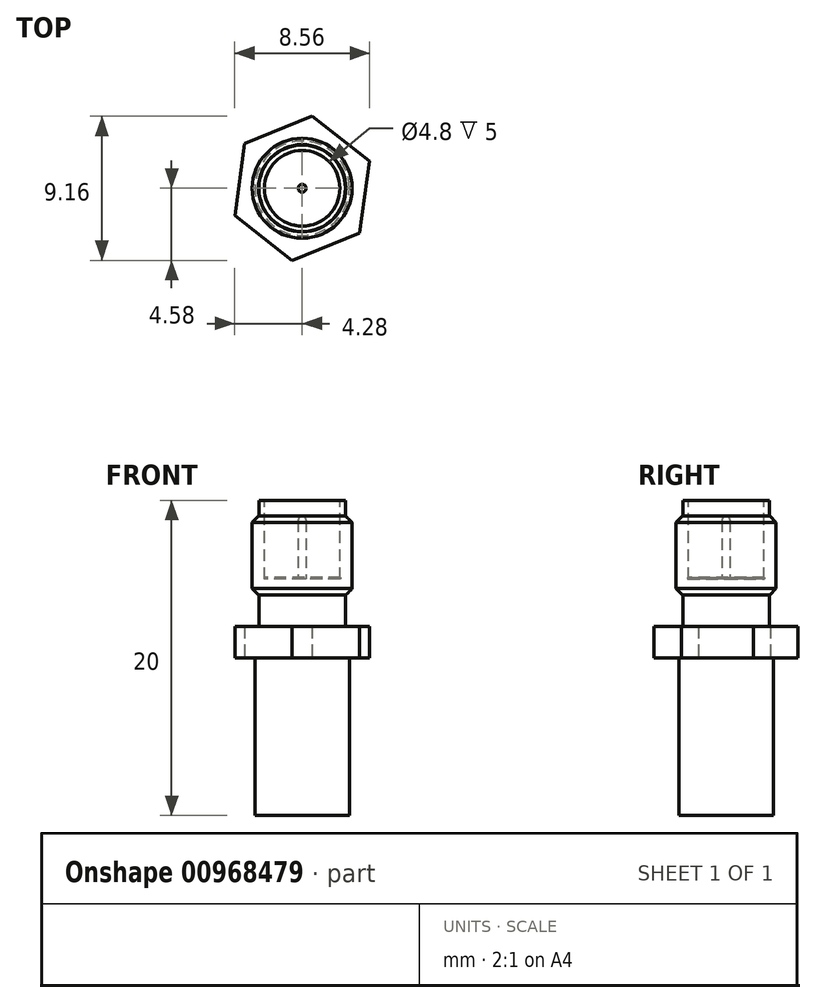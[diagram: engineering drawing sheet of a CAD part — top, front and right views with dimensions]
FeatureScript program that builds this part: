
annotation { "Feature Type Name" : "Feature", "Feature Type Description" : "" }
export const myFeature = defineFeature(function(context is Context, id is Id, definition is map)
    precondition{}
    {
        {
            var Q0;
            Q0=qCreatedBy(makeId("Top.planeOp"),FACE);
            var sketch = newSketch(context, id + "F0", { "sketchPlane" : qUnion([Q0])});
            skCircle(sketch, "E0.cCircle", {"center": v(0, 0) * mm, "radius": 4 * mm, "construction": true});
            skLineSegment(sketch, "E0.0", {"start": v(-3.65, 2.83) * mm, "end": v(0.63, 4.58) * mm});
            skLineSegment(sketch, "E0.1", {"start": v(0.63, 4.58) * mm, "end": v(4.28, 1.74) * mm});
            skLineSegment(sketch, "E0.2", {"start": v(4.28, 1.74) * mm, "end": v(3.65, -2.83) * mm});
            skLineSegment(sketch, "E0.3", {"start": v(3.65, -2.83) * mm, "end": v(-0.63, -4.58) * mm});
            skLineSegment(sketch, "E0.4", {"start": v(-0.63, -4.58) * mm, "end": v(-4.28, -1.74) * mm});
            skLineSegment(sketch, "E0.5", {"start": v(-4.28, -1.74) * mm, "end": v(-3.65, 2.83) * mm});
            skPoint(sketch, "E0.0.midPoint", {"position": v(-1.5, 3.7) * mm});
            skSolve(sketch);
        }
        {
            var Q0;
            Q0 = qSketchRegion(id + "F0", true);
            extrude(context, id + "F1", {"entities" : qUnion([Q0]), "depth" : 2 * mm, "offsetDistance" : 25 * mm});
        }
        {
            var Q0;
            Q0=makeQuery(id+"F1.opExtrude","CAP_FACE",FACE,{"disambiguationData":[OSD([sQuery(id+"F0.wireOp",EDGE,"E0.0"),sQuery(id+"F0.wireOp",EDGE,"E0.1"),sQuery(id+"F0.wireOp",EDGE,"E0.2"),sQuery(id+"F0.wireOp",EDGE,"E0.3"),sQuery(id+"F0.wireOp",EDGE,"E0.4"),sQuery(id+"F0.wireOp",EDGE,"E0.5")])],"isStart":false});
            var sketch = newSketch(context, id + "F2", { "sketchPlane" : qUnion([Q0])});
            skCircle(sketch, "E1", {"center": v(0, 0) * mm, "radius": 2.75 * mm});
            skSolve(sketch);
        }
        {
            var Q0;
            Q0 = qSketchRegion(id + "F2", true);
            extrude(context, id + "F3", {"entities" : qUnion([Q0]), "operationType" : NewBodyOperationType.ADD, "depth" : 2 * mm, "offsetDistance" : 25 * mm});
        }
        {
            var Q0;
            Q0=makeQuery(id+"F3.opExtrude","CAP_FACE",FACE,{"disambiguationData":[OSD([sQuery(id+"F2.wireOp",EDGE,"E1")])],"isStart":false});
            var sketch = newSketch(context, id + "F4", { "sketchPlane" : qUnion([Q0])});
            skCircle(sketch, "E2", {"center": v(0, 0) * mm, "radius": 3.17 * mm});
            skSolve(sketch);
        }
        {
            var Q0;
            Q0 = qSketchRegion(id + "F4", true);
            extrude(context, id + "F5", {"entities" : qUnion([Q0]), "operationType" : NewBodyOperationType.ADD, "depth" : 5 * mm, "offsetDistance" : 25 * mm});
        }
        {
            var Q0;
            Q0=makeQuery(id+"F5.opExtrude","CAP_FACE",FACE,{"disambiguationData":[OSD([sQuery(id+"F4.wireOp",EDGE,"E2")])],"isStart":false});
            var sketch = newSketch(context, id + "F6", { "sketchPlane" : qUnion([Q0])});
            skCircle(sketch, "E3", {"center": v(0, 0) * mm, "radius": 2.75 * mm});
            skSolve(sketch);
        }
        {
            var Q0;
            Q0 = qSketchRegion(id + "F6", true);
            extrude(context, id + "F7", {"entities" : qUnion([Q0]), "operationType" : NewBodyOperationType.ADD, "depth" : 1 * mm, "offsetDistance" : 25 * mm});
        }
        {
            var Q0;
            Q0=makeQuery(id+"F5.opExtrude","CAP_EDGE",EDGE,{"disambiguationData":[OSD([sQuery(id+"F4.wireOp",EDGE,"E2")])],"isStart":false});
            chamfer(context, id + "F8", {"entities" : qUnion([Q0]), "width" : .4 * mm, "tangentPropagation" : true});
        }
        {
            var Q0;
            Q0=makeQuery(id+"F5.opExtrude","CAP_EDGE",EDGE,{"disambiguationData":[OSD([sQuery(id+"F4.wireOp",EDGE,"E2")])],"isStart":true});
            chamfer(context, id + "F9", {"entities" : qUnion([Q0]), "width" : .4 * mm, "tangentPropagation" : true});
        }
        {
            var Q0;
            Q0=makeQuery(id+"F7.opExtrude","CAP_FACE",FACE,{"disambiguationData":[OSD([sQuery(id+"F6.wireOp",EDGE,"E3")])],"isStart":false});
            var sketch = newSketch(context, id + "F10", { "sketchPlane" : qUnion([Q0])});
            skCircle(sketch, "E4", {"center": v(0, 0) * mm, "radius": 2.4 * mm});
            skSolve(sketch);
        }
        {
            var Q0;
            Q0 = qSketchRegion(id + "F10", true);
            extrude(context, id + "F11", {"entities" : qUnion([Q0]), "operationType" : NewBodyOperationType.REMOVE, "oppositeDirection" : true, "depth" : 5 * mm, "offsetDistance" : 25 * mm});
        }
        {
            var Q0;
            Q0=makeQuery(id+"F11.boolean.opBoolean","COPY",FACE,{"derivedFrom":makeQuery(id+"F11.opExtrude","CAP_FACE",FACE,{"disambiguationData":[OSD([sQuery(id+"F10.wireOp",EDGE,"E4")])],"isStart":false})});
            var sketch = newSketch(context, id + "F12", { "sketchPlane" : qUnion([Q0])});
            skCircle(sketch, "E5", {"center": v(0, 0) * mm, "radius": 0.25 * mm});
            skSolve(sketch);
        }
        {
            var Q0;
            Q0 = qSketchRegion(id + "F12", true);
            extrude(context, id + "F13", {"entities" : qUnion([Q0]), "operationType" : NewBodyOperationType.ADD, "depth" : 4 * mm, "offsetDistance" : 25 * mm});
        }
        {
            var Q0;
            Q0=makeQuery(id+"F13.opExtrude","CAP_EDGE",EDGE,{"disambiguationData":[OSD([sQuery(id+"F12.wireOp",EDGE,"E5")])],"isStart":false});
            fillet(context, id + "F14", {"entities" : qUnion([Q0]), "radius" : .25 * mm, "tangentPropagation" : true, "allowEdgeOverflow" : false});
        }
        {
            var Q0;
            Q0=makeQuery(id+"F1.opExtrude","CAP_FACE",FACE,{"disambiguationData":[OSD([sQuery(id+"F0.wireOp",EDGE,"E0.0"),sQuery(id+"F0.wireOp",EDGE,"E0.1"),sQuery(id+"F0.wireOp",EDGE,"E0.2"),sQuery(id+"F0.wireOp",EDGE,"E0.3"),sQuery(id+"F0.wireOp",EDGE,"E0.4"),sQuery(id+"F0.wireOp",EDGE,"E0.5")])],"isStart":true});
            var sketch = newSketch(context, id + "F15", { "sketchPlane" : qUnion([Q0])});
            skCircle(sketch, "E6", {"center": v(0, 0) * mm, "radius": 3 * mm});
            skSolve(sketch);
        }
        {
            var Q0;
            Q0 = qSketchRegion(id + "F15", true);
            extrude(context, id + "F16", {"entities" : qUnion([Q0]), "depth" : 10 * mm, "offsetDistance" : 25 * mm});
        }
        {
            var Q0;
            Q0=makeQuery(id+"F11.boolean.opBoolean","COPY",FACE,{"derivedFrom":makeQuery(id+"F11.opExtrude","CAP_FACE",FACE,{"disambiguationData":[OSD([sQuery(id+"F10.wireOp",EDGE,"E4")])],"isStart":false})});
            var sketch = newSketch(context, id + "F17", { "sketchPlane" : qUnion([Q0])});
            skCircle(sketch, "E7", {"center": v(0, 0) * mm, "radius": 2.44 * mm});
            skSolve(sketch);
        }
        {
            var Q0;
            Q0 = qSketchRegion(id + "F17", true);
            extrude(context, id + "F18", {"entities" : qUnion([Q0]), "depth" : .1 * mm, "offsetDistance" : 25 * mm});
        }
    });
